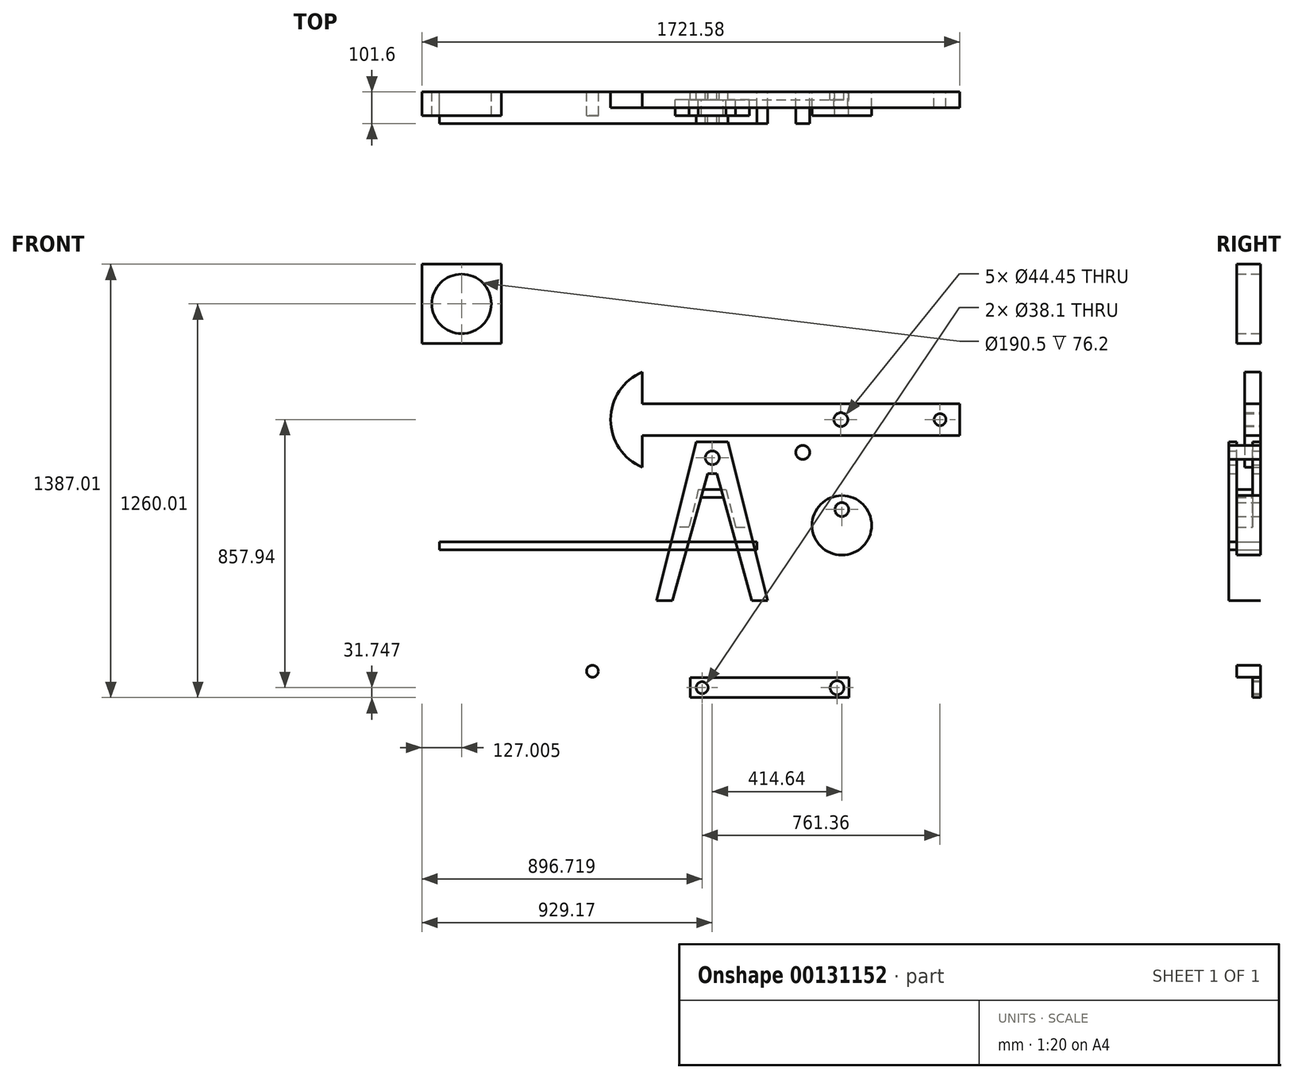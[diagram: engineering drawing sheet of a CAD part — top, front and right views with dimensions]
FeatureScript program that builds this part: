
annotation { "Feature Type Name" : "Feature", "Feature Type Description" : "" }
export const myFeature = defineFeature(function(context is Context, id is Id, definition is map)
    precondition{}
    {
        {
            var Q0;
            Q0=qCreatedBy(makeId("Front.planeOp"),FACE);
            var sketch = newSketch(context, id + "F0", { "sketchPlane" : qUnion([Q0])});
            skLineSegment(sketch, "E0.bottom", {"start": v(-341.21, 176.93) * mm, "end": v(674.79, 176.93) * mm});
            skLineSegment(sketch, "E0.top", {"start": v(-341.21, 75.33) * mm, "end": v(674.79, 75.33) * mm});
            skLineSegment(sketch, "E0.right", {"start": v(674.79, 176.93) * mm, "end": v(674.79, 75.33) * mm});
            skLineSegment(sketch, "E1", {"start": v(-341.21, 278.53) * mm, "end": v(-341.21, 176.93) * mm});
            skPoint(sketch, "E2", {"position": v(-341.21, 126.13) * mm});
            skArc(sketch, "E3", {"start": v(-341.21, 278.53) * mm, "mid": v(-442.81, 126.13) * mm, "end": v(-341.21, -26.27) * mm});
            skLineSegment(sketch, "E4.trimOffspring", {"start": v(-341.21, 75.33) * mm, "end": v(-341.21, -26.27) * mm});
            skPoint(sketch, "E5", {"position": v(611.29, 126.13) * mm});
            skPoint(sketch, "E5.positionSnap0", {"position": v(674.79, 126.13) * mm});
            skCircle(sketch, "E6", {"center": v(611.29, 126.13) * mm, "radius": 19.05 * mm});
            skPoint(sketch, "E7", {"position": v(293.79, 126.13) * mm});
            skCircle(sketch, "E8", {"center": v(293.79, 126.13) * mm, "radius": 22.23 * mm});
            skSolve(sketch);
        }
        {
            var Q0;
            Q0=makeQuery(id+"F0.imprint","IMPRINT",FACE,{"disambiguationData":[TD([[makeQuery(id+"F0.imprint","IMPRINT",EDGE,{"derivedFrom":sQuery(id+"F0.wireOp",EDGE,"E0.bottom")}),-1.0]])]});
            extrude(context, id + "F1", {"entities" : qUnion([Q0]), "depth" : 50.8 * mm});
        }
        {
            var Q0;
            Q0=qCreatedBy(makeId("Front.planeOp"),FACE);
            var sketch = newSketch(context, id + "F2", { "sketchPlane" : qUnion([Q0])});
            skLineSegment(sketch, "E9.bottom", {"start": v(-168.42, 54.74) * mm, "end": v(-117.62, 54.74) * mm});
            skLineSegment(sketch, "E10.bottom", {"start": v(-117.62, 54.74) * mm, "end": v(-66.82, 54.74) * mm});
            skLineSegment(sketch, "E11", {"start": v(-117.62, 54.74) * mm, "end": v(-168.42, 54.74) * mm});
            skLineSegment(sketch, "E12", {"start": v(-168.42, 54.74) * mm, "end": v(-295.42, -453.26) * mm});
            skLineSegment(sketch, "E13", {"start": v(-295.42, -453.26) * mm, "end": v(-244.62, -453.26) * mm});
            skLineSegment(sketch, "E14", {"start": v(-244.62, -453.26) * mm, "end": v(-131.73, -46.86) * mm});
            skLineSegment(sketch, "E15", {"start": v(-103.5, -46.86) * mm, "end": v(9.38, -453.26) * mm});
            skLineSegment(sketch, "E16", {"start": v(9.38, -453.26) * mm, "end": v(60.18, -453.26) * mm});
            skLineSegment(sketch, "E17", {"start": v(60.18, -453.26) * mm, "end": v(-66.82, 54.74) * mm});
            skPoint(sketch, "E18.orphan", {"position": v(-117.62, -453.26) * mm});
            skLineSegment(sketch, "E19", {"start": v(-131.73, -46.86) * mm, "end": v(-103.5, -46.86) * mm});
            skPoint(sketch, "E20.end.orphan", {"position": v(-117.62, -46.86) * mm});
            skPoint(sketch, "E9.right.end.orphan", {"position": v(-117.62, 3.94) * mm});
            skCircle(sketch, "E21", {"center": v(-117.62, 3.94) * mm, "radius": 22.23 * mm});
            skSolve(sketch);
        }
        {
            var Q0;
            Q0=makeQuery(id+"F2.imprint","IMPRINT",FACE,{"disambiguationData":[TD([[makeQuery(id+"F2.imprint","IMPRINT",EDGE,{"derivedFrom":sQuery(id+"F2.wireOp",EDGE,"E10.bottom")}),-1.0]])]});
            extrude(context, id + "F3", {"entities" : qUnion([Q0]), "depth" : 25.4 * mm});
        }
        {
            var Q0;
            Q0=makeQuery(id+"F3.opExtrude","CAP_FACE",FACE,{"disambiguationData":[OSD([sQuery(id+"F2.wireOp",EDGE,"E10.bottom"),sQuery(id+"F2.wireOp",EDGE,"E11"),sQuery(id+"F2.wireOp",EDGE,"E12"),sQuery(id+"F2.wireOp",EDGE,"E13"),sQuery(id+"F2.wireOp",EDGE,"E14"),sQuery(id+"F2.wireOp",EDGE,"E15"),sQuery(id+"F2.wireOp",EDGE,"E16"),sQuery(id+"F2.wireOp",EDGE,"E17"),sQuery(id+"F2.wireOp",EDGE,"E19"),sQuery(id+"F2.wireOp",EDGE,"E21")])],"isStart":false});
            var sketch = newSketch(context, id + "F4", { "sketchPlane" : qUnion([Q0])});
            skLineSegment(sketch, "E22", {"start": v(-135.08, -40.5) * mm, "end": v(-103.28, -40.5) * mm});
            skLineSegment(sketch, "E23", {"start": v(-135.08, -40.5) * mm, "end": v(-147.78, -40.5) * mm});
            skLineSegment(sketch, "E24", {"start": v(-147.78, -40.5) * mm, "end": v(-90.58, -40.5) * mm});
            skLineSegment(sketch, "E25", {"start": v(-103.28, -40.5) * mm, "end": v(-90.58, -40.5) * mm});
            skLineSegment(sketch, "E26", {"start": v(-131.73, -46.86) * mm, "end": v(-103.5, -46.86) * mm});
            skPoint(sketch, "E27.end.orphan", {"position": v(-131.73, -90.43) * mm});
            skPoint(sketch, "E28.end.orphan", {"position": v(-90.58, -90.43) * mm});
            skLineSegment(sketch, "E29", {"start": v(-162.07, -97.66) * mm, "end": v(-192.23, -218.3) * mm});
            skLineSegment(sketch, "E30", {"start": v(-192.23, -218.3) * mm, "end": v(-236.68, -218.3) * mm});
            skLineSegment(sketch, "E31", {"start": v(-43, -218.3) * mm, "end": v(1.44, -218.3) * mm});
            skPoint(sketch, "E32.orphan", {"position": v(-192.23, -40.5) * mm});
            skLineSegment(sketch, "E33", {"start": v(-162.07, -97.66) * mm, "end": v(-73.17, -97.66) * mm});
            skPoint(sketch, "E34.start.orphan", {"position": v(-37.47, -97.66) * mm});
            skPoint(sketch, "E35.orphan", {"position": v(-57.19, -97.66) * mm});
            skLineSegment(sketch, "E36", {"start": v(-73.17, -97.66) * mm, "end": v(-43, -218.3) * mm});
            skLineSegment(sketch, "E37", {"start": v(-73.17, -97.66) * mm, "end": v(-28.72, -97.66) * mm});
            skLineSegment(sketch, "E38", {"start": v(-152.9, -123.06) * mm, "end": v(-82.34, -123.06) * mm});
            skLineSegment(sketch, "E39", {"start": v(-82.34, -123.06) * mm, "end": v(9.38, -453.26) * mm});
            skLineSegment(sketch, "E40", {"start": v(9.38, -453.26) * mm, "end": v(60.18, -453.26) * mm});
            skLineSegment(sketch, "E41", {"start": v(60.18, -453.26) * mm, "end": v(1.44, -218.3) * mm});
            skLineSegment(sketch, "E42", {"start": v(-236.68, -218.3) * mm, "end": v(-295.42, -453.26) * mm});
            skLineSegment(sketch, "E43", {"start": v(-295.42, -453.26) * mm, "end": v(-244.62, -453.26) * mm});
            skLineSegment(sketch, "E44", {"start": v(-244.62, -453.26) * mm, "end": v(-152.9, -123.06) * mm});
            skSolve(sketch);
        }
        {
            var Q0;
            {var subQ5=sQuery(id+"F4.wireOp",EDGE,"E31");Q0=makeQuery(id+"F4.imprint","IMPRINT",FACE,{"disambiguationData":[TD([[makeQuery(id+"F4.imprint","IMPRINT",EDGE,{"derivedFrom":subQ5}),-1.0]])]});}
            var Q1;
            {var subQ2=sQuery(id+"F4.wireOp",EDGE,"E29");Q1=makeQuery(id+"F4.imprint","IMPRINT",FACE,{"disambiguationData":[TD([[makeQuery(id+"F4.imprint","IMPRINT",EDGE,{"derivedFrom":subQ2}),1.0]])]});}
            var Q2;
            {var subQ5=sQuery(id+"F4.wireOp",EDGE,"E38");Q2=makeQuery(id+"F4.imprint","IMPRINT",FACE,{"disambiguationData":[TD([[makeQuery(id+"F4.imprint","IMPRINT",EDGE,{"derivedFrom":subQ5}),1.0]])]});}
            extrude(context, id + "F5", {"entities" : qUnion([Q0, Q1, Q2]), "operationType" : NewBodyOperationType.ADD, "depth" : 50.8 * mm});
        }
        {
            var Q0;
            Q0=makeQuery(id+"F5.opExtrude","CAP_FACE",FACE,{"disambiguationData":[OSD([sQuery(id+"F4.wireOp",EDGE,"E29"),sQuery(id+"F4.wireOp",EDGE,"E30"),sQuery(id+"F4.wireOp",EDGE,"E31"),sQuery(id+"F4.wireOp",EDGE,"E33"),sQuery(id+"F4.wireOp",EDGE,"E36"),sQuery(id+"F4.wireOp",EDGE,"E38"),sQuery(id+"F4.wireOp",EDGE,"E39"),sQuery(id+"F4.wireOp",EDGE,"E40"),sQuery(id+"F4.wireOp",EDGE,"E41"),sQuery(id+"F4.wireOp",EDGE,"E42"),sQuery(id+"F4.wireOp",EDGE,"E43"),sQuery(id+"F4.wireOp",EDGE,"E44")])],"isStart":false});
            var sketch = newSketch(context, id + "F6", { "sketchPlane" : qUnion([Q0])});
            skLineSegment(sketch, "E45", {"start": v(60.18, -453.26) * mm, "end": v(-66.82, 54.74) * mm});
            skLineSegment(sketch, "E46", {"start": v(-295.42, -453.26) * mm, "end": v(-168.42, 54.74) * mm});
            skLineSegment(sketch, "E47", {"start": v(-168.42, 54.74) * mm, "end": v(-66.82, 54.74) * mm});
            skLineSegment(sketch, "E48", {"start": v(-158.32, -142.58) * mm, "end": v(-131.73, -46.86) * mm});
            skLineSegment(sketch, "E49", {"start": v(-74.73, -150.47) * mm, "end": v(-103.5, -46.86) * mm});
            skLineSegment(sketch, "E50", {"start": v(-103.5, -46.86) * mm, "end": v(-131.73, -46.86) * mm});
            skLineSegment(sketch, "E51", {"start": v(-117.62, 54.74) * mm, "end": v(-117.62, 3.94) * mm});
            skCircle(sketch, "E52", {"center": v(-117.62, 3.94) * mm, "radius": 22.23 * mm});
            skSolve(sketch);
        }
        {
            var Q0;
            {var subQ0=sQuery(id+"F6.wireOp",EDGE,"E47");Q0=makeQuery(id+"F6.imprint","IMPRINT",FACE,{"disambiguationData":[TD([[makeQuery(id+"F6.imprint","IMPRINT",EDGE,{"derivedFrom":subQ0}),-1.0]])]});}
            var Q1;
            Q1=makeQuery(id+"F6.imprint","IMPRINT",FACE,{"disambiguationData":[TD([[makeQuery(id+"F6.imprint","IMPRINT",EDGE,{"derivedFrom":makeQuery(id+"F5.opExtrude","CAP_EDGE",EDGE,{"disambiguationData":[OSD([sQuery(id+"F4.wireOp",EDGE,"E29")])],"isStart":false})}),1.0]])]});
            var Q2;
            {var subQ0=makeQuery(id+"F5.opExtrude","CAP_EDGE",EDGE,{"disambiguationData":[OSD([sQuery(id+"F4.wireOp",EDGE,"E31")])],"isStart":false});Q2=makeQuery(id+"F6.imprint","IMPRINT",FACE,{"disambiguationData":[TD([[makeQuery(id+"F6.imprint","IMPRINT",EDGE,{"derivedFrom":subQ0}),-1.0]])]});}
            extrude(context, id + "F7", {"entities" : qUnion([Q0, Q1, Q2]), "operationType" : NewBodyOperationType.ADD, "depth" : 25.4 * mm});
        }
        {
            var Q0;
            Q0=qCreatedBy(makeId("Front.planeOp"),FACE);
            var sketch = newSketch(context, id + "F8", { "sketchPlane" : qUnion([Q0])});
            skCircle(sketch, "E53", {"center": v(171.97, 21.09) * mm, "radius": 22.23 * mm});
            skSolve(sketch);
        }
        {
            var Q0;
            Q0=makeQuery(id+"F8.imprint","IMPRINT",FACE,{"disambiguationData":[TD([[makeQuery(id+"F8.imprint","IMPRINT",EDGE,{"derivedFrom":sQuery(id+"F8.wireOp",EDGE,"E53")}),1.0]])]});
            extrude(context, id + "F9", {"entities" : qUnion([Q0]), "depth" : 101.6 * mm});
        }
        {
            var Q0;
            Q0=qCreatedBy(makeId("Front.planeOp"),FACE);
            var sketch = newSketch(context, id + "F10", { "sketchPlane" : qUnion([Q0])});
            skCircle(sketch, "E54", {"center": v(297.02, -212.32) * mm, "radius": 95.25 * mm});
            skCircle(sketch, "E55", {"center": v(297.02, -161.52) * mm, "radius": 22.23 * mm});
            skSolve(sketch);
        }
        {
            var Q0;
            Q0=makeQuery(id+"F10.imprint","IMPRINT",FACE,{"disambiguationData":[TD([[makeQuery(id+"F10.imprint","IMPRINT",EDGE,{"derivedFrom":sQuery(id+"F10.wireOp",EDGE,"E54")}),1.0]])]});
            extrude(context, id + "F11", {"entities" : qUnion([Q0]), "depth" : 76.2 * mm});
        }
        {
            var Q0;
            Q0=qCreatedBy(makeId("Front.planeOp"),FACE);
            var sketch = newSketch(context, id + "F12", { "sketchPlane" : qUnion([Q0])});
            skCircle(sketch, "E56", {"center": v(-501, -679.07) * mm, "radius": 19.05 * mm});
            skSolve(sketch);
        }
        {
            var Q0;
            Q0=makeQuery(id+"F12.imprint","IMPRINT",FACE,{"disambiguationData":[TD([[makeQuery(id+"F12.imprint","IMPRINT",EDGE,{"derivedFrom":sQuery(id+"F12.wireOp",EDGE,"E56")}),1.0]])]});
            extrude(context, id + "F13", {"entities" : qUnion([Q0]), "depth" : 76.2 * mm});
        }
        {
            var Q0;
            Q0=qCreatedBy(makeId("Front.planeOp"),FACE);
            var sketch = newSketch(context, id + "F14", { "sketchPlane" : qUnion([Q0])});
            skLineSegment(sketch, "E57.bottom", {"start": v(-188.17, -700.06) * mm, "end": v(319.83, -700.06) * mm});
            skLineSegment(sketch, "E57.top", {"start": v(-188.17, -763.56) * mm, "end": v(319.83, -763.56) * mm});
            skLineSegment(sketch, "E57.left", {"start": v(-188.17, -700.06) * mm, "end": v(-188.17, -763.56) * mm});
            skLineSegment(sketch, "E57.right", {"start": v(319.83, -700.06) * mm, "end": v(319.83, -763.56) * mm});
            skLineSegment(sketch, "E58", {"start": v(-188.17, -731.81) * mm, "end": v(65.83, -731.81) * mm});
            skPoint(sketch, "E58.endSnap0", {"position": v(65.83, -700.06) * mm});
            skLineSegment(sketch, "E59", {"start": v(65.83, -731.81) * mm, "end": v(-61.17, -731.81) * mm});
            skLineSegment(sketch, "E60", {"start": v(-188.17, -731.81) * mm, "end": v(-150.07, -731.81) * mm});
            skCircle(sketch, "E61", {"center": v(-150.07, -731.81) * mm, "radius": 19.05 * mm});
            skLineSegment(sketch, "E62", {"start": v(319.83, -731.81) * mm, "end": v(281.73, -731.81) * mm});
            skCircle(sketch, "E63", {"center": v(281.73, -731.81) * mm, "radius": 22.23 * mm});
            skLineSegment(sketch, "E64", {"start": v(-111.97, -700.06) * mm, "end": v(-111.97, -763.56) * mm});
            skLineSegment(sketch, "E65", {"start": v(243.63, -700.06) * mm, "end": v(243.63, -763.56) * mm});
            skSolve(sketch);
        }
        {
            var Q0;
            {var subQ6=sQuery(id+"F14.wireOp",EDGE,"E65");Q0=makeQuery(id+"F14.imprint","IMPRINT",FACE,{"disambiguationData":[TD([[makeQuery(id+"F14.imprint","IMPRINT",EDGE,{"derivedFrom":subQ6}),-1.0]])]});}
            var Q1;
            {var subQ1=sQuery(id+"F14.wireOp",EDGE,"E57.left");var subQ9=sQuery(id+"F14.wireOp",EDGE,"E57.top");var subQ10=makeQuery(id+"F14.imprint","INTERSECT",VERTEX,{"derivedFrom":[subQ9,subQ1]});Q1=makeQuery(id+"F14.imprint","IMPRINT",FACE,{"disambiguationData":[TD([[makeQuery(id+"F14.imprint","IMPRINT",EDGE,{"disambiguationData":[TD([[subQ10,-1.0]])],"derivedFrom":subQ9}),1.0]])]});}
            var Q2;
            {var subQ6=sQuery(id+"F14.wireOp",EDGE,"E57.left");var subQ9=sQuery(id+"F14.wireOp",EDGE,"E57.bottom");var subQ10=makeQuery(id+"F14.imprint","INTERSECT",VERTEX,{"derivedFrom":[subQ9,subQ6]});Q2=makeQuery(id+"F14.imprint","IMPRINT",FACE,{"disambiguationData":[TD([[makeQuery(id+"F14.imprint","IMPRINT",EDGE,{"disambiguationData":[TD([[subQ10,-1.0]])],"derivedFrom":subQ9}),-1.0]])]});}
            var Q3;
            Q3=makeQuery(id+"F14.imprint","IMPRINT",FACE,{"disambiguationData":[TD([[makeQuery(id+"F14.imprint","IMPRINT",EDGE,{"derivedFrom":sQuery(id+"F14.wireOp",EDGE,"E63")}),-1.0]])]});
            extrude(context, id + "F15", {"entities" : qUnion([Q0, Q1, Q2, Q3]), "depth" : 25.4 * mm});
        }
        {
            var Q0;
            Q0=qCreatedBy(makeId("Front.planeOp"),FACE);
            var sketch = newSketch(context, id + "F16", { "sketchPlane" : qUnion([Q0])});
            skLineSegment(sketch, "E66.bottom", {"start": v(-1046.79, 623.45) * mm, "end": v(-792.79, 623.45) * mm});
            skLineSegment(sketch, "E66.top", {"start": v(-1046.79, 369.45) * mm, "end": v(-792.79, 369.45) * mm});
            skLineSegment(sketch, "E66.left", {"start": v(-1046.79, 623.45) * mm, "end": v(-1046.79, 369.45) * mm});
            skLineSegment(sketch, "E66.right", {"start": v(-792.79, 623.45) * mm, "end": v(-792.79, 369.45) * mm});
            skPoint(sketch, "E67", {"position": v(-919.79, 496.45) * mm});
            skPoint(sketch, "E67.positionSnap0", {"position": v(-792.79, 496.45) * mm});
            skPoint(sketch, "E67.positionSnap1", {"position": v(-919.79, 623.45) * mm});
            skCircle(sketch, "E68", {"center": v(-919.79, 496.45) * mm, "radius": 95.25 * mm});
            skSolve(sketch);
        }
        {
            var Q0;
            Q0=makeQuery(id+"F16.imprint","IMPRINT",FACE,{"disambiguationData":[TD([[makeQuery(id+"F16.imprint","IMPRINT",EDGE,{"derivedFrom":sQuery(id+"F16.wireOp",EDGE,"E66.bottom")}),-1.0]])]});
            extrude(context, id + "F17", {"entities" : qUnion([Q0]), "depth" : 76.2 * mm});
        }
        {
            var Q0;
            Q0=qCreatedBy(makeId("Front.planeOp"),FACE);
            var sketch = newSketch(context, id + "F18", { "sketchPlane" : qUnion([Q0])});
            skLineSegment(sketch, "E69.bottom", {"start": v(24.68, -264.95) * mm, "end": v(-991.32, -264.95) * mm});
            skLineSegment(sketch, "E69.top", {"start": v(24.68, -290.35) * mm, "end": v(-991.32, -290.35) * mm});
            skLineSegment(sketch, "E69.left", {"start": v(24.68, -264.95) * mm, "end": v(24.68, -290.35) * mm});
            skLineSegment(sketch, "E69.right", {"start": v(-991.32, -264.95) * mm, "end": v(-991.32, -290.35) * mm});
            skSolve(sketch);
        }
        {
            var Q0;
            Q0=makeQuery(id+"F18.imprint","IMPRINT",FACE,{"disambiguationData":[TD([[makeQuery(id+"F18.imprint","IMPRINT",EDGE,{"derivedFrom":sQuery(id+"F18.wireOp",EDGE,"E69.bottom")}),1.0]])]});
            extrude(context, id + "F19", {"entities" : qUnion([Q0]), "depth" : 101.6 * mm});
        }
    });
